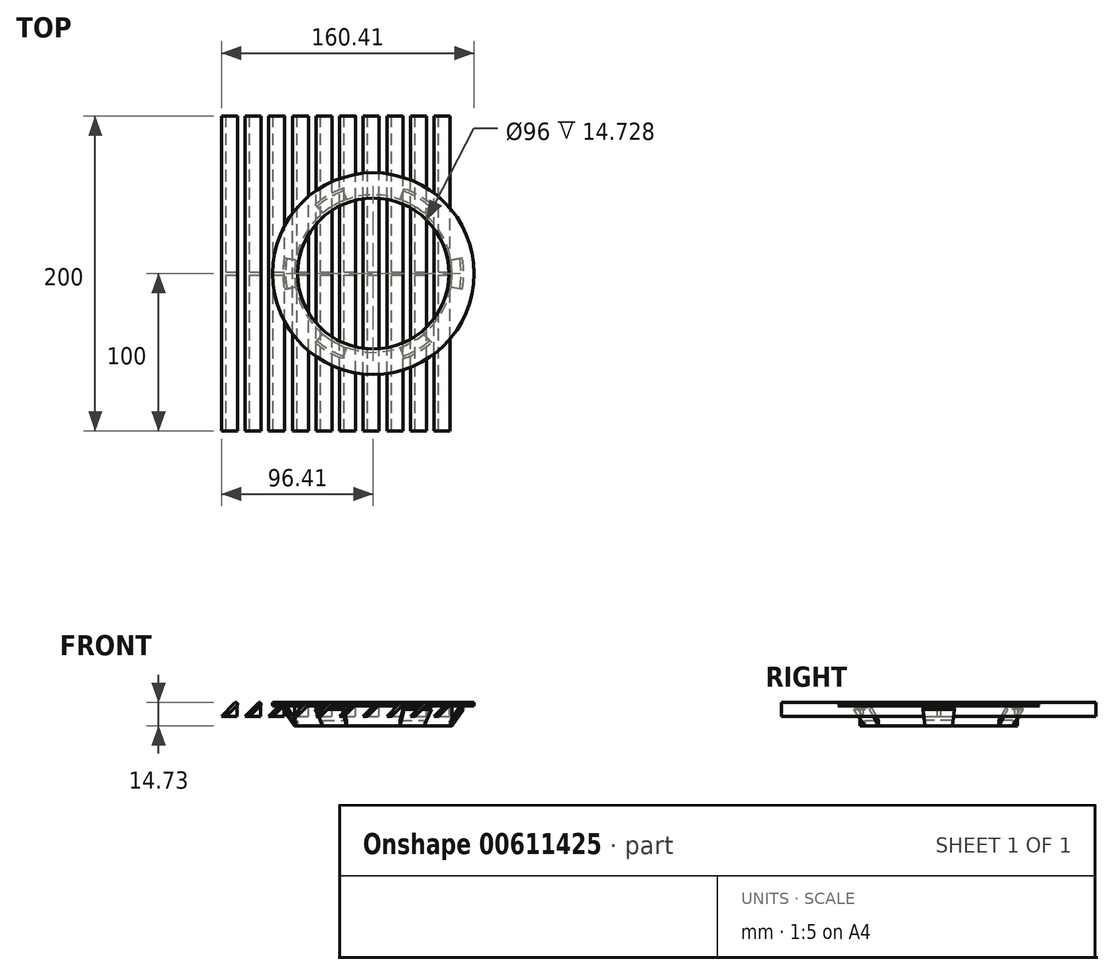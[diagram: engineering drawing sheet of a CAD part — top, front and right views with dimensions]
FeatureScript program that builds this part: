
annotation { "Feature Type Name" : "Feature", "Feature Type Description" : "" }
export const myFeature = defineFeature(function(context is Context, id is Id, definition is map)
    precondition{}
    {
        {
            var Q0;
            Q0=qCreatedBy(makeId("Front.planeOp"),FACE);
            var sketch = newSketch(context, id + "F0", { "sketchPlane" : qUnion([Q0])});
            skLineSegment(sketch, "E0", {"start": v(-100.7, 1.7) * mm, "end": v(-87.98, 14.44) * mm});
            skLineSegment(sketch, "E1", {"start": v(-99.3, 0.3) * mm, "end": v(-86.56, 13.02) * mm});
            skArc(sketch, "E2", {"start": v(-86.56, 13.02) * mm, "mid": v(-86.56, 14.44) * mm, "end": v(-87.98, 14.44) * mm});
            skArc(sketch, "E3", {"start": v(-100.7, 1.7) * mm, "mid": v(-100.7, 0.3) * mm, "end": v(-99.3, 0.3) * mm});
            skLineSegment(sketch, "E4", {"start": v(-43.9, 0) * mm, "end": v(34.53, 0) * mm, "construction": true});
            skLineSegment(sketch, "E5.1.0.0", {"start": v(-84.3, 0.3) * mm, "end": v(-71.56, 13.02) * mm});
            skLineSegment(sketch, "E5.1.0.1", {"start": v(-85.7, 1.7) * mm, "end": v(-72.98, 14.44) * mm});
            skArc(sketch, "E5.1.0.2", {"start": v(-71.56, 13.02) * mm, "mid": v(-71.56, 14.44) * mm, "end": v(-72.98, 14.44) * mm});
            skArc(sketch, "E5.1.0.3", {"start": v(-85.7, 1.7) * mm, "mid": v(-85.7, 0.3) * mm, "end": v(-84.3, 0.3) * mm});
            skLineSegment(sketch, "E5.2.0.0", {"start": v(-69.3, 0.3) * mm, "end": v(-56.56, 13.02) * mm});
            skLineSegment(sketch, "E5.2.0.1", {"start": v(-70.7, 1.7) * mm, "end": v(-57.98, 14.44) * mm});
            skArc(sketch, "E5.2.0.2", {"start": v(-56.56, 13.02) * mm, "mid": v(-56.56, 14.44) * mm, "end": v(-57.98, 14.44) * mm});
            skArc(sketch, "E5.2.0.3", {"start": v(-70.7, 1.7) * mm, "mid": v(-70.7, 0.3) * mm, "end": v(-69.3, 0.3) * mm});
            skLineSegment(sketch, "E5.3.0.0", {"start": v(-54.3, 0.3) * mm, "end": v(-41.56, 13.02) * mm});
            skLineSegment(sketch, "E5.3.0.1", {"start": v(-55.7, 1.7) * mm, "end": v(-42.98, 14.44) * mm});
            skArc(sketch, "E5.3.0.2", {"start": v(-41.56, 13.02) * mm, "mid": v(-41.56, 14.44) * mm, "end": v(-42.98, 14.44) * mm});
            skArc(sketch, "E5.3.0.3", {"start": v(-55.7, 1.7) * mm, "mid": v(-55.7, 0.3) * mm, "end": v(-54.3, 0.3) * mm});
            skLineSegment(sketch, "E5.4.0.0", {"start": v(-39.3, 0.3) * mm, "end": v(-26.56, 13.02) * mm});
            skLineSegment(sketch, "E5.4.0.1", {"start": v(-40.7, 1.7) * mm, "end": v(-27.98, 14.44) * mm});
            skArc(sketch, "E5.4.0.2", {"start": v(-26.56, 13.02) * mm, "mid": v(-26.56, 14.44) * mm, "end": v(-27.98, 14.44) * mm});
            skArc(sketch, "E5.4.0.3", {"start": v(-40.7, 1.7) * mm, "mid": v(-40.7, 0.3) * mm, "end": v(-39.3, 0.3) * mm});
            skLineSegment(sketch, "E5.5.0.0", {"start": v(-24.3, 0.3) * mm, "end": v(-11.56, 13.02) * mm});
            skLineSegment(sketch, "E5.5.0.1", {"start": v(-25.7, 1.7) * mm, "end": v(-12.98, 14.44) * mm});
            skArc(sketch, "E5.5.0.2", {"start": v(-11.56, 13.02) * mm, "mid": v(-11.56, 14.44) * mm, "end": v(-12.98, 14.44) * mm});
            skArc(sketch, "E5.5.0.3", {"start": v(-25.7, 1.7) * mm, "mid": v(-25.7, 0.3) * mm, "end": v(-24.3, 0.3) * mm});
            skLineSegment(sketch, "E5.6.0.0", {"start": v(-9.3, 0.3) * mm, "end": v(3.44, 13.02) * mm});
            skLineSegment(sketch, "E5.6.0.1", {"start": v(-10.7, 1.7) * mm, "end": v(2.02, 14.44) * mm});
            skArc(sketch, "E5.6.0.2", {"start": v(3.44, 13.02) * mm, "mid": v(3.44, 14.44) * mm, "end": v(2.02, 14.44) * mm});
            skArc(sketch, "E5.6.0.3", {"start": v(-10.7, 1.7) * mm, "mid": v(-10.7, 0.3) * mm, "end": v(-9.3, 0.3) * mm});
            skLineSegment(sketch, "E5.7.0.0", {"start": v(5.7, 0.3) * mm, "end": v(18.44, 13.02) * mm});
            skLineSegment(sketch, "E5.7.0.1", {"start": v(4.3, 1.7) * mm, "end": v(17.02, 14.44) * mm});
            skArc(sketch, "E5.7.0.2", {"start": v(18.44, 13.02) * mm, "mid": v(18.44, 14.44) * mm, "end": v(17.02, 14.44) * mm});
            skArc(sketch, "E5.7.0.3", {"start": v(4.3, 1.7) * mm, "mid": v(4.3, 0.3) * mm, "end": v(5.7, 0.3) * mm});
            skLineSegment(sketch, "E5.8.0.0", {"start": v(20.7, 0.3) * mm, "end": v(33.44, 13.02) * mm});
            skLineSegment(sketch, "E5.8.0.1", {"start": v(19.3, 1.7) * mm, "end": v(32.02, 14.44) * mm});
            skArc(sketch, "E5.8.0.2", {"start": v(33.44, 13.02) * mm, "mid": v(33.44, 14.44) * mm, "end": v(32.02, 14.44) * mm});
            skArc(sketch, "E5.8.0.3", {"start": v(19.3, 1.7) * mm, "mid": v(19.3, 0.3) * mm, "end": v(20.7, 0.3) * mm});
            skLineSegment(sketch, "E5.9.0.0", {"start": v(35.7, 0.3) * mm, "end": v(48.44, 13.02) * mm});
            skLineSegment(sketch, "E5.9.0.1", {"start": v(34.3, 1.7) * mm, "end": v(47.02, 14.44) * mm});
            skArc(sketch, "E5.9.0.2", {"start": v(48.44, 13.02) * mm, "mid": v(48.44, 14.44) * mm, "end": v(47.02, 14.44) * mm});
            skArc(sketch, "E5.9.0.3", {"start": v(34.3, 1.7) * mm, "mid": v(34.3, 0.3) * mm, "end": v(35.7, 0.3) * mm});
            skLineSegment(sketch, "E5.direction1", {"start": v(-99.3, 0.3) * mm, "end": v(-84.3, 0.3) * mm, "construction": true});
            skLineSegment(sketch, "E6", {"start": v(-100, 1) * mm, "end": v(-100, 0) * mm});
            skLineSegment(sketch, "E7.bottom", {"start": v(-110.02, 0) * mm, "end": v(120.53, 0) * mm});
            skLineSegment(sketch, "E7.top", {"start": v(-110.02, 6) * mm, "end": v(120.53, 6) * mm});
            skLineSegment(sketch, "E7.left", {"start": v(-110.02, 0) * mm, "end": v(-110.02, 6) * mm});
            skLineSegment(sketch, "E7.right", {"start": v(120.53, 0) * mm, "end": v(120.53, 6) * mm});
            skLineSegment(sketch, "E8", {"start": v(-86.56, 13.02) * mm, "end": v(-86.56, 6) * mm});
            skLineSegment(sketch, "E9", {"start": v(-86.56, 6) * mm, "end": v(-93.59, 6) * mm});
            skLineSegment(sketch, "E10", {"start": v(-93.59, 6) * mm, "end": v(-86.56, 13.02) * mm});
            skLineSegment(sketch, "E11.1.0.0", {"start": v(-71.56, 13.02) * mm, "end": v(-71.56, 6) * mm});
            skLineSegment(sketch, "E11.1.0.1", {"start": v(-71.56, 6) * mm, "end": v(-78.59, 6) * mm});
            skLineSegment(sketch, "E11.1.0.2", {"start": v(-78.59, 6) * mm, "end": v(-71.56, 13.02) * mm});
            skLineSegment(sketch, "E11.2.0.0", {"start": v(-56.56, 13.02) * mm, "end": v(-56.56, 6) * mm});
            skLineSegment(sketch, "E11.2.0.1", {"start": v(-56.56, 6) * mm, "end": v(-63.59, 6) * mm});
            skLineSegment(sketch, "E11.2.0.2", {"start": v(-63.59, 6) * mm, "end": v(-56.56, 13.02) * mm});
            skLineSegment(sketch, "E11.3.0.0", {"start": v(-41.56, 13.02) * mm, "end": v(-41.56, 6) * mm});
            skLineSegment(sketch, "E11.3.0.1", {"start": v(-41.56, 6) * mm, "end": v(-48.59, 6) * mm});
            skLineSegment(sketch, "E11.3.0.2", {"start": v(-48.59, 6) * mm, "end": v(-41.56, 13.02) * mm});
            skLineSegment(sketch, "E11.4.0.0", {"start": v(-26.56, 13.02) * mm, "end": v(-26.56, 6) * mm});
            skLineSegment(sketch, "E11.4.0.1", {"start": v(-26.56, 6) * mm, "end": v(-33.59, 6) * mm});
            skLineSegment(sketch, "E11.4.0.2", {"start": v(-33.59, 6) * mm, "end": v(-26.56, 13.02) * mm});
            skLineSegment(sketch, "E11.5.0.0", {"start": v(-11.56, 13.02) * mm, "end": v(-11.56, 6) * mm});
            skLineSegment(sketch, "E11.5.0.1", {"start": v(-11.56, 6) * mm, "end": v(-18.59, 6) * mm});
            skLineSegment(sketch, "E11.5.0.2", {"start": v(-18.59, 6) * mm, "end": v(-11.56, 13.02) * mm});
            skLineSegment(sketch, "E11.6.0.0", {"start": v(3.44, 13.02) * mm, "end": v(3.44, 6) * mm});
            skLineSegment(sketch, "E11.6.0.1", {"start": v(3.44, 6) * mm, "end": v(-3.59, 6) * mm});
            skLineSegment(sketch, "E11.6.0.2", {"start": v(-3.59, 6) * mm, "end": v(3.44, 13.02) * mm});
            skLineSegment(sketch, "E11.7.0.0", {"start": v(18.44, 13.02) * mm, "end": v(18.44, 6) * mm});
            skLineSegment(sketch, "E11.7.0.1", {"start": v(18.44, 6) * mm, "end": v(11.41, 6) * mm});
            skLineSegment(sketch, "E11.7.0.2", {"start": v(11.41, 6) * mm, "end": v(18.44, 13.02) * mm});
            skLineSegment(sketch, "E11.8.0.0", {"start": v(33.44, 13.02) * mm, "end": v(33.44, 6) * mm});
            skLineSegment(sketch, "E11.8.0.1", {"start": v(33.44, 6) * mm, "end": v(26.41, 6) * mm});
            skLineSegment(sketch, "E11.8.0.2", {"start": v(26.41, 6) * mm, "end": v(33.44, 13.02) * mm});
            skLineSegment(sketch, "E11.9.0.0", {"start": v(48.44, 13.02) * mm, "end": v(48.44, 6) * mm});
            skLineSegment(sketch, "E11.9.0.1", {"start": v(48.44, 6) * mm, "end": v(41.41, 6) * mm});
            skLineSegment(sketch, "E11.9.0.2", {"start": v(41.41, 6) * mm, "end": v(48.44, 13.02) * mm});
            skLineSegment(sketch, "E11.direction1", {"start": v(-86.56, 6) * mm, "end": v(-71.56, 6) * mm, "construction": true});
            skSolve(sketch);
        }
        {
            var Q0;
            {var subQ0=sQuery(id+"F0.wireOp",EDGE,"E7.left");Q0=makeQuery(id+"F0.imprint","IMPRINT",FACE,{"disambiguationData":[TD([[makeQuery(id+"F0.imprint","IMPRINT",EDGE,{"derivedFrom":subQ0}),-1.0]])]});}
            var Q1;
            {var subQ4=sQuery(id+"F0.wireOp",EDGE,"E1");Q1=makeQuery(id+"F0.imprint","IMPRINT",FACE,{"disambiguationData":[TD([[makeQuery(id+"F0.imprint","IMPRINT",EDGE,{"derivedFrom":subQ4}),1.0]])]});}
            var Q2;
            {var subQ6=sQuery(id+"F0.wireOp",EDGE,"E1");Q2=makeQuery(id+"F0.imprint","IMPRINT",FACE,{"disambiguationData":[TD([[makeQuery(id+"F0.imprint","IMPRINT",EDGE,{"derivedFrom":subQ6}),-1.0]])]});}
            var Q3;
            {var subQ6=sQuery(id+"F0.wireOp",EDGE,"E5.1.0.0");Q3=makeQuery(id+"F0.imprint","IMPRINT",FACE,{"disambiguationData":[TD([[makeQuery(id+"F0.imprint","IMPRINT",EDGE,{"derivedFrom":subQ6}),1.0]])]});}
            var Q4;
            {var subQ8=sQuery(id+"F0.wireOp",EDGE,"E5.1.0.0");Q4=makeQuery(id+"F0.imprint","IMPRINT",FACE,{"disambiguationData":[TD([[makeQuery(id+"F0.imprint","IMPRINT",EDGE,{"derivedFrom":subQ8}),-1.0]])]});}
            var Q5;
            {var subQ6=sQuery(id+"F0.wireOp",EDGE,"E5.2.0.0");Q5=makeQuery(id+"F0.imprint","IMPRINT",FACE,{"disambiguationData":[TD([[makeQuery(id+"F0.imprint","IMPRINT",EDGE,{"derivedFrom":subQ6}),1.0]])]});}
            var Q6;
            {var subQ10=sQuery(id+"F0.wireOp",EDGE,"E5.2.0.0");Q6=makeQuery(id+"F0.imprint","IMPRINT",FACE,{"disambiguationData":[TD([[makeQuery(id+"F0.imprint","IMPRINT",EDGE,{"derivedFrom":subQ10}),-1.0]])]});}
            var Q7;
            {var subQ6=sQuery(id+"F0.wireOp",EDGE,"E5.3.0.0");Q7=makeQuery(id+"F0.imprint","IMPRINT",FACE,{"disambiguationData":[TD([[makeQuery(id+"F0.imprint","IMPRINT",EDGE,{"derivedFrom":subQ6}),1.0]])]});}
            var Q8;
            {var subQ8=sQuery(id+"F0.wireOp",EDGE,"E5.3.0.0");Q8=makeQuery(id+"F0.imprint","IMPRINT",FACE,{"disambiguationData":[TD([[makeQuery(id+"F0.imprint","IMPRINT",EDGE,{"derivedFrom":subQ8}),-1.0]])]});}
            var Q9;
            {var subQ6=sQuery(id+"F0.wireOp",EDGE,"E5.4.0.0");Q9=makeQuery(id+"F0.imprint","IMPRINT",FACE,{"disambiguationData":[TD([[makeQuery(id+"F0.imprint","IMPRINT",EDGE,{"derivedFrom":subQ6}),1.0]])]});}
            var Q10;
            {var subQ8=sQuery(id+"F0.wireOp",EDGE,"E5.4.0.0");Q10=makeQuery(id+"F0.imprint","IMPRINT",FACE,{"disambiguationData":[TD([[makeQuery(id+"F0.imprint","IMPRINT",EDGE,{"derivedFrom":subQ8}),-1.0]])]});}
            var Q11;
            {var subQ8=sQuery(id+"F0.wireOp",EDGE,"E5.5.0.0");Q11=makeQuery(id+"F0.imprint","IMPRINT",FACE,{"disambiguationData":[TD([[makeQuery(id+"F0.imprint","IMPRINT",EDGE,{"derivedFrom":subQ8}),-1.0]])]});}
            var Q12;
            {var subQ8=sQuery(id+"F0.wireOp",EDGE,"E5.6.0.0");Q12=makeQuery(id+"F0.imprint","IMPRINT",FACE,{"disambiguationData":[TD([[makeQuery(id+"F0.imprint","IMPRINT",EDGE,{"derivedFrom":subQ8}),-1.0]])]});}
            var Q13;
            {var subQ6=sQuery(id+"F0.wireOp",EDGE,"E5.5.0.0");Q13=makeQuery(id+"F0.imprint","IMPRINT",FACE,{"disambiguationData":[TD([[makeQuery(id+"F0.imprint","IMPRINT",EDGE,{"derivedFrom":subQ6}),1.0]])]});}
            var Q14;
            {var subQ6=sQuery(id+"F0.wireOp",EDGE,"E5.9.0.0");Q14=makeQuery(id+"F0.imprint","IMPRINT",FACE,{"disambiguationData":[TD([[makeQuery(id+"F0.imprint","IMPRINT",EDGE,{"derivedFrom":subQ6}),-1.0]])]});}
            var Q15;
            {var subQ5=sQuery(id+"F0.wireOp",EDGE,"E5.6.0.0");Q15=makeQuery(id+"F0.imprint","IMPRINT",FACE,{"disambiguationData":[TD([[makeQuery(id+"F0.imprint","IMPRINT",EDGE,{"derivedFrom":subQ5}),1.0]])]});}
            var Q16;
            {var subQ8=sQuery(id+"F0.wireOp",EDGE,"E5.7.0.0");Q16=makeQuery(id+"F0.imprint","IMPRINT",FACE,{"disambiguationData":[TD([[makeQuery(id+"F0.imprint","IMPRINT",EDGE,{"derivedFrom":subQ8}),-1.0]])]});}
            var Q17;
            {var subQ6=sQuery(id+"F0.wireOp",EDGE,"E5.7.0.0");Q17=makeQuery(id+"F0.imprint","IMPRINT",FACE,{"disambiguationData":[TD([[makeQuery(id+"F0.imprint","IMPRINT",EDGE,{"derivedFrom":subQ6}),1.0]])]});}
            var Q18;
            {var subQ6=sQuery(id+"F0.wireOp",EDGE,"E5.9.0.0");Q18=makeQuery(id+"F0.imprint","IMPRINT",FACE,{"disambiguationData":[TD([[makeQuery(id+"F0.imprint","IMPRINT",EDGE,{"derivedFrom":subQ6}),1.0]])]});}
            var Q19;
            {var subQ9=sQuery(id+"F0.wireOp",EDGE,"E5.8.0.0");Q19=makeQuery(id+"F0.imprint","IMPRINT",FACE,{"disambiguationData":[TD([[makeQuery(id+"F0.imprint","IMPRINT",EDGE,{"derivedFrom":subQ9}),-1.0]])]});}
            var Q20;
            {var subQ6=sQuery(id+"F0.wireOp",EDGE,"E5.8.0.0");Q20=makeQuery(id+"F0.imprint","IMPRINT",FACE,{"disambiguationData":[TD([[makeQuery(id+"F0.imprint","IMPRINT",EDGE,{"derivedFrom":subQ6}),1.0]])]});}
            var Q21;
            Q21=makeQuery(id+"F0.imprint","IMPRINT",FACE,{"disambiguationData":[TD([[makeQuery(id+"F0.imprint","IMPRINT",EDGE,{"derivedFrom":sQuery(id+"F0.wireOp",EDGE,"E11.9.0.0")}),-1.0]])]});
            var Q22;
            Q22=makeQuery(id+"F0.imprint","IMPRINT",FACE,{"disambiguationData":[TD([[makeQuery(id+"F0.imprint","IMPRINT",EDGE,{"derivedFrom":sQuery(id+"F0.wireOp",EDGE,"E11.8.0.0")}),-1.0]])]});
            var Q23;
            Q23=makeQuery(id+"F0.imprint","IMPRINT",FACE,{"disambiguationData":[TD([[makeQuery(id+"F0.imprint","IMPRINT",EDGE,{"derivedFrom":sQuery(id+"F0.wireOp",EDGE,"E11.7.0.0")}),-1.0]])]});
            var Q24;
            Q24=makeQuery(id+"F0.imprint","IMPRINT",FACE,{"disambiguationData":[TD([[makeQuery(id+"F0.imprint","IMPRINT",EDGE,{"derivedFrom":sQuery(id+"F0.wireOp",EDGE,"E11.6.0.0")}),-1.0]])]});
            var Q25;
            Q25=makeQuery(id+"F0.imprint","IMPRINT",FACE,{"disambiguationData":[TD([[makeQuery(id+"F0.imprint","IMPRINT",EDGE,{"derivedFrom":sQuery(id+"F0.wireOp",EDGE,"E11.5.0.0")}),-1.0]])]});
            var Q26;
            Q26=makeQuery(id+"F0.imprint","IMPRINT",FACE,{"disambiguationData":[TD([[makeQuery(id+"F0.imprint","IMPRINT",EDGE,{"derivedFrom":sQuery(id+"F0.wireOp",EDGE,"E11.4.0.0")}),-1.0]])]});
            var Q27;
            Q27=makeQuery(id+"F0.imprint","IMPRINT",FACE,{"disambiguationData":[TD([[makeQuery(id+"F0.imprint","IMPRINT",EDGE,{"derivedFrom":sQuery(id+"F0.wireOp",EDGE,"E11.3.0.0")}),-1.0]])]});
            var Q28;
            Q28=makeQuery(id+"F0.imprint","IMPRINT",FACE,{"disambiguationData":[TD([[makeQuery(id+"F0.imprint","IMPRINT",EDGE,{"derivedFrom":sQuery(id+"F0.wireOp",EDGE,"E11.2.0.0")}),-1.0]])]});
            var Q29;
            Q29=makeQuery(id+"F0.imprint","IMPRINT",FACE,{"disambiguationData":[TD([[makeQuery(id+"F0.imprint","IMPRINT",EDGE,{"derivedFrom":sQuery(id+"F0.wireOp",EDGE,"E11.1.0.0")}),-1.0]])]});
            var Q30;
            Q30=makeQuery(id+"F0.imprint","IMPRINT",FACE,{"disambiguationData":[TD([[makeQuery(id+"F0.imprint","IMPRINT",EDGE,{"derivedFrom":sQuery(id+"F0.wireOp",EDGE,"E8")}),-1.0]])]});
            extrude(context, id + "F1", {"entities" : qUnion([Q0, Q1, Q2, Q3, Q4, Q5, Q6, Q7, Q8, Q9, Q10, Q11, Q12, Q13, Q14, Q15, Q16, Q17, Q18, Q19, Q20, Q21, Q22, Q23, Q24, Q25, Q26, Q27, Q28, Q29, Q30]), "endBound" : BoundingType.SYMMETRIC, "depth" : 2 * mm, "offsetDistance" : 25 * mm});
        }
        {
            var Q0;
            {var subQ0=sQuery(id+"F0.wireOp",EDGE,"E2");Q0=makeQuery(id+"F0.imprint","IMPRINT",FACE,{"disambiguationData":[TD([[makeQuery(id+"F0.imprint","IMPRINT",EDGE,{"derivedFrom":subQ0}),1.0]])]});}
            var Q1;
            {var subQ0=sQuery(id+"F0.wireOp",EDGE,"E5.1.0.2");Q1=makeQuery(id+"F0.imprint","IMPRINT",FACE,{"disambiguationData":[TD([[makeQuery(id+"F0.imprint","IMPRINT",EDGE,{"derivedFrom":subQ0}),1.0]])]});}
            var Q2;
            {var subQ4=sQuery(id+"F0.wireOp",EDGE,"E1");Q2=makeQuery(id+"F0.imprint","IMPRINT",FACE,{"disambiguationData":[TD([[makeQuery(id+"F0.imprint","IMPRINT",EDGE,{"derivedFrom":subQ4}),1.0]])]});}
            var Q3;
            {var subQ6=sQuery(id+"F0.wireOp",EDGE,"E5.1.0.0");Q3=makeQuery(id+"F0.imprint","IMPRINT",FACE,{"disambiguationData":[TD([[makeQuery(id+"F0.imprint","IMPRINT",EDGE,{"derivedFrom":subQ6}),1.0]])]});}
            var Q4;
            {var subQ6=sQuery(id+"F0.wireOp",EDGE,"E5.2.0.0");Q4=makeQuery(id+"F0.imprint","IMPRINT",FACE,{"disambiguationData":[TD([[makeQuery(id+"F0.imprint","IMPRINT",EDGE,{"derivedFrom":subQ6}),1.0]])]});}
            var Q5;
            {var subQ0=sQuery(id+"F0.wireOp",EDGE,"E5.2.0.2");Q5=makeQuery(id+"F0.imprint","IMPRINT",FACE,{"disambiguationData":[TD([[makeQuery(id+"F0.imprint","IMPRINT",EDGE,{"derivedFrom":subQ0}),1.0]])]});}
            var Q6;
            {var subQ0=sQuery(id+"F0.wireOp",EDGE,"E5.3.0.2");Q6=makeQuery(id+"F0.imprint","IMPRINT",FACE,{"disambiguationData":[TD([[makeQuery(id+"F0.imprint","IMPRINT",EDGE,{"derivedFrom":subQ0}),1.0]])]});}
            var Q7;
            {var subQ6=sQuery(id+"F0.wireOp",EDGE,"E5.3.0.0");Q7=makeQuery(id+"F0.imprint","IMPRINT",FACE,{"disambiguationData":[TD([[makeQuery(id+"F0.imprint","IMPRINT",EDGE,{"derivedFrom":subQ6}),1.0]])]});}
            var Q8;
            {var subQ0=sQuery(id+"F0.wireOp",EDGE,"E5.4.0.2");Q8=makeQuery(id+"F0.imprint","IMPRINT",FACE,{"disambiguationData":[TD([[makeQuery(id+"F0.imprint","IMPRINT",EDGE,{"derivedFrom":subQ0}),1.0]])]});}
            var Q9;
            {var subQ6=sQuery(id+"F0.wireOp",EDGE,"E5.4.0.0");Q9=makeQuery(id+"F0.imprint","IMPRINT",FACE,{"disambiguationData":[TD([[makeQuery(id+"F0.imprint","IMPRINT",EDGE,{"derivedFrom":subQ6}),1.0]])]});}
            var Q10;
            {var subQ0=sQuery(id+"F0.wireOp",EDGE,"E5.5.0.2");Q10=makeQuery(id+"F0.imprint","IMPRINT",FACE,{"disambiguationData":[TD([[makeQuery(id+"F0.imprint","IMPRINT",EDGE,{"derivedFrom":subQ0}),1.0]])]});}
            var Q11;
            {var subQ6=sQuery(id+"F0.wireOp",EDGE,"E5.5.0.0");Q11=makeQuery(id+"F0.imprint","IMPRINT",FACE,{"disambiguationData":[TD([[makeQuery(id+"F0.imprint","IMPRINT",EDGE,{"derivedFrom":subQ6}),1.0]])]});}
            var Q12;
            {var subQ0=sQuery(id+"F0.wireOp",EDGE,"E5.6.0.2");Q12=makeQuery(id+"F0.imprint","IMPRINT",FACE,{"disambiguationData":[TD([[makeQuery(id+"F0.imprint","IMPRINT",EDGE,{"derivedFrom":subQ0}),1.0]])]});}
            var Q13;
            {var subQ5=sQuery(id+"F0.wireOp",EDGE,"E5.6.0.0");Q13=makeQuery(id+"F0.imprint","IMPRINT",FACE,{"disambiguationData":[TD([[makeQuery(id+"F0.imprint","IMPRINT",EDGE,{"derivedFrom":subQ5}),1.0]])]});}
            var Q14;
            {var subQ0=sQuery(id+"F0.wireOp",EDGE,"E5.7.0.2");Q14=makeQuery(id+"F0.imprint","IMPRINT",FACE,{"disambiguationData":[TD([[makeQuery(id+"F0.imprint","IMPRINT",EDGE,{"derivedFrom":subQ0}),1.0]])]});}
            var Q15;
            {var subQ6=sQuery(id+"F0.wireOp",EDGE,"E5.7.0.0");Q15=makeQuery(id+"F0.imprint","IMPRINT",FACE,{"disambiguationData":[TD([[makeQuery(id+"F0.imprint","IMPRINT",EDGE,{"derivedFrom":subQ6}),1.0]])]});}
            var Q16;
            {var subQ0=sQuery(id+"F0.wireOp",EDGE,"E5.9.0.2");Q16=makeQuery(id+"F0.imprint","IMPRINT",FACE,{"disambiguationData":[TD([[makeQuery(id+"F0.imprint","IMPRINT",EDGE,{"derivedFrom":subQ0}),1.0]])]});}
            var Q17;
            {var subQ6=sQuery(id+"F0.wireOp",EDGE,"E5.9.0.0");Q17=makeQuery(id+"F0.imprint","IMPRINT",FACE,{"disambiguationData":[TD([[makeQuery(id+"F0.imprint","IMPRINT",EDGE,{"derivedFrom":subQ6}),1.0]])]});}
            var Q18;
            {var subQ0=sQuery(id+"F0.wireOp",EDGE,"E5.8.0.2");Q18=makeQuery(id+"F0.imprint","IMPRINT",FACE,{"disambiguationData":[TD([[makeQuery(id+"F0.imprint","IMPRINT",EDGE,{"derivedFrom":subQ0}),1.0]])]});}
            var Q19;
            {var subQ6=sQuery(id+"F0.wireOp",EDGE,"E5.8.0.0");Q19=makeQuery(id+"F0.imprint","IMPRINT",FACE,{"disambiguationData":[TD([[makeQuery(id+"F0.imprint","IMPRINT",EDGE,{"derivedFrom":subQ6}),1.0]])]});}
            extrude(context, id + "F2", {"entities" : qUnion([Q0, Q1, Q2, Q3, Q4, Q5, Q6, Q7, Q8, Q9, Q10, Q11, Q12, Q13, Q14, Q15, Q16, Q17, Q18, Q19]), "operationType" : NewBodyOperationType.ADD, "endBound" : BoundingType.SYMMETRIC, "depth" : 200 * mm, "offsetDistance" : 25 * mm});
        }
        {
            var Q0;
            Q0=qCreatedBy(makeId("Front.planeOp"),FACE);
            var sketch = newSketch(context, id + "F3", { "sketchPlane" : qUnion([Q0])});
            skLineSegment(sketch, "E12", {"start": v(-48, 0) * mm, "end": v(-48, 14.73) * mm});
            skLineSegment(sketch, "E13", {"start": v(-48, 14.73) * mm, "end": v(-64, 14.73) * mm});
            skLineSegment(sketch, "E14", {"start": v(-64, 14.73) * mm, "end": v(-64, 12.73) * mm});
            skLineSegment(sketch, "E15", {"start": v(-64, 12.73) * mm, "end": v(-50, 12.73) * mm});
            skLineSegment(sketch, "E16", {"start": v(-50, 12.73) * mm, "end": v(-50, 0) * mm});
            skLineSegment(sketch, "E17", {"start": v(-50, 0) * mm, "end": v(-48, 0) * mm});
            skLineSegment(sketch, "E18.bottom", {"start": v(-48, 0) * mm, "end": v(0, 0) * mm});
            skLineSegment(sketch, "E18.top", {"start": v(-48, 14.73) * mm, "end": v(0, 14.73) * mm});
            skLineSegment(sketch, "E18.right", {"start": v(0, 0) * mm, "end": v(0, 14.73) * mm});
            skSolve(sketch);
        }
        {
            var Q0;
            Q0=makeQuery(id+"F3.imprint","IMPRINT",FACE,{"disambiguationData":[TD([[makeQuery(id+"F3.imprint","IMPRINT",EDGE,{"derivedFrom":sQuery(id+"F3.wireOp",EDGE,"E18.bottom")}),1.0]])]});
            var Q1;
            Q1=sQuery(id+"F3.wireOp",EDGE,"E18.right");
            revolve(context, id + "F4", {"entities" : qUnion([Q0]), "axis" : qUnion([Q1]), "revolveType" : RevolveType.FULL});
        }
        {
            var Q0;
            Q0=makeQuery(id+"F3.imprint","IMPRINT",FACE,{"disambiguationData":[TD([[makeQuery(id+"F3.imprint","IMPRINT",EDGE,{"derivedFrom":sQuery(id+"F3.wireOp",EDGE,"E13")}),1.0]])]});
            var Q1;
            Q1=sQuery(id+"F3.wireOp",EDGE,"E18.right");
            revolve(context, id + "F5", {"entities" : qUnion([Q0]), "axis" : qUnion([Q1]), "revolveType" : RevolveType.FULL});
        }
        {
            var Q0;
            Q0=makeQuery(id+"F1.opExtrude","SWEPT_BODY",BODY,{"disambiguationData":[OSD([sQuery(id+"F0.wireOp",EDGE,"E7.bottom"),sQuery(id+"F0.wireOp",EDGE,"E7.top"),sQuery(id+"F0.wireOp",EDGE,"E7.left"),sQuery(id+"F0.wireOp",EDGE,"E7.right"),sQuery(id+"F0.wireOp",EDGE,"E8"),sQuery(id+"F0.wireOp",EDGE,"E10"),sQuery(id+"F0.wireOp",EDGE,"E11.1.0.0"),sQuery(id+"F0.wireOp",EDGE,"E11.1.0.2"),sQuery(id+"F0.wireOp",EDGE,"E11.2.0.0"),sQuery(id+"F0.wireOp",EDGE,"E11.2.0.2"),sQuery(id+"F0.wireOp",EDGE,"E11.3.0.0"),sQuery(id+"F0.wireOp",EDGE,"E11.3.0.2"),sQuery(id+"F0.wireOp",EDGE,"E11.4.0.0"),sQuery(id+"F0.wireOp",EDGE,"E11.4.0.2"),sQuery(id+"F0.wireOp",EDGE,"E11.5.0.0"),sQuery(id+"F0.wireOp",EDGE,"E11.5.0.2"),sQuery(id+"F0.wireOp",EDGE,"E11.6.0.0"),sQuery(id+"F0.wireOp",EDGE,"E11.6.0.2"),sQuery(id+"F0.wireOp",EDGE,"E11.7.0.0"),sQuery(id+"F0.wireOp",EDGE,"E11.7.0.2"),sQuery(id+"F0.wireOp",EDGE,"E11.8.0.0"),sQuery(id+"F0.wireOp",EDGE,"E11.8.0.2"),sQuery(id+"F0.wireOp",EDGE,"E11.9.0.0"),sQuery(id+"F0.wireOp",EDGE,"E11.9.0.2")])]});
            var Q1;
            Q1=makeQuery(id+"F4.opRevolve","SWEPT_BODY",BODY,{"disambiguationData":[OSD([sQuery(id+"F3.wireOp",EDGE,"E18.bottom"),sQuery(id+"F3.wireOp",EDGE,"E18.top"),sQuery(id+"F3.wireOp",EDGE,"E12"),sQuery(id+"F3.wireOp",EDGE,"E18.right")])]});
            booleanBodies(context, id + "F6", {"operationType" : BooleanOperationType.INTERSECTION, "tools" : qUnion([Q0, Q1])});
        }
        {
            var Q0;
            Q0=qCreatedBy(makeId("Front.planeOp"),FACE);
            var sketch = newSketch(context, id + "F7", { "sketchPlane" : qUnion([Q0])});
            skLineSegment(sketch, "E19", {"start": v(-50, 0) * mm, "end": v(-57.37, 10.53) * mm});
            skLineSegment(sketch, "E20", {"start": v(-57.37, 10.53) * mm, "end": v(-55.74, 11.68) * mm});
            skLineSegment(sketch, "E21", {"start": v(-55.74, 11.68) * mm, "end": v(-50, 3.49) * mm});
            skLineSegment(sketch, "E22", {"start": v(-50, 3.49) * mm, "end": v(-50, 0) * mm});
            skSolve(sketch);
        }
        {
            var Q0;
            Q0=makeQuery(id+"F7.imprint","IMPRINT",FACE,{"disambiguationData":[TD([[makeQuery(id+"F7.imprint","IMPRINT",EDGE,{"derivedFrom":sQuery(id+"F7.wireOp",EDGE,"E19")}),-1.0]])]});
            var Q1;
            Q1=sQuery(id+"F3.wireOp",EDGE,"E18.right");
            revolve(context, id + "F8", {"entities" : qUnion([Q0]), "axis" : qUnion([Q1]), "revolveType" : RevolveType.SYMMETRIC, "angle" : 20 * degree});
        }
        {
            var Q0;
            Q0=makeQuery(id+"F8.opRevolve","SWEPT_BODY",BODY,{"disambiguationData":[OSD([sQuery(id+"F7.wireOp",EDGE,"w5AzRqgL-sx4R-0zAU-fVmm-IlFLUkx6vCTs"),sQuery(id+"F7.wireOp",EDGE,"krVzm16z-fuV2-qBHl-n2Yh-v5c2BJakqTgH"),sQuery(id+"F7.wireOp",EDGE,"bjGqZoSP-U1ZC-EEri-Inb0-MHFNUvgYmz5N"),sQuery(id+"F7.wireOp",EDGE,"zZm2DvFa-ee1F-au5e-hMwC-PsnCrLQKuOH5")])]});
            var Q1;
            Q1=makeQuery(id+"F8.opRevolve","SWEPT_BODY",BODY,{"disambiguationData":[OSD([sQuery(id+"F7.wireOp",EDGE,"E19"),sQuery(id+"F7.wireOp",EDGE,"E20"),sQuery(id+"F7.wireOp",EDGE,"E21"),sQuery(id+"F7.wireOp",EDGE,"E22")])]});
            var Q2;
            Q2=sQuery(id+"F3.wireOp",EDGE,"E18.right");
            circularPattern(context, id + "F9", {"entities" : qUnion([Q0, Q1]), "axis" : qUnion([Q2]), "angle" : 360 * degree, "instanceCount" : 6, "equalSpace" : true});
        }
    });
